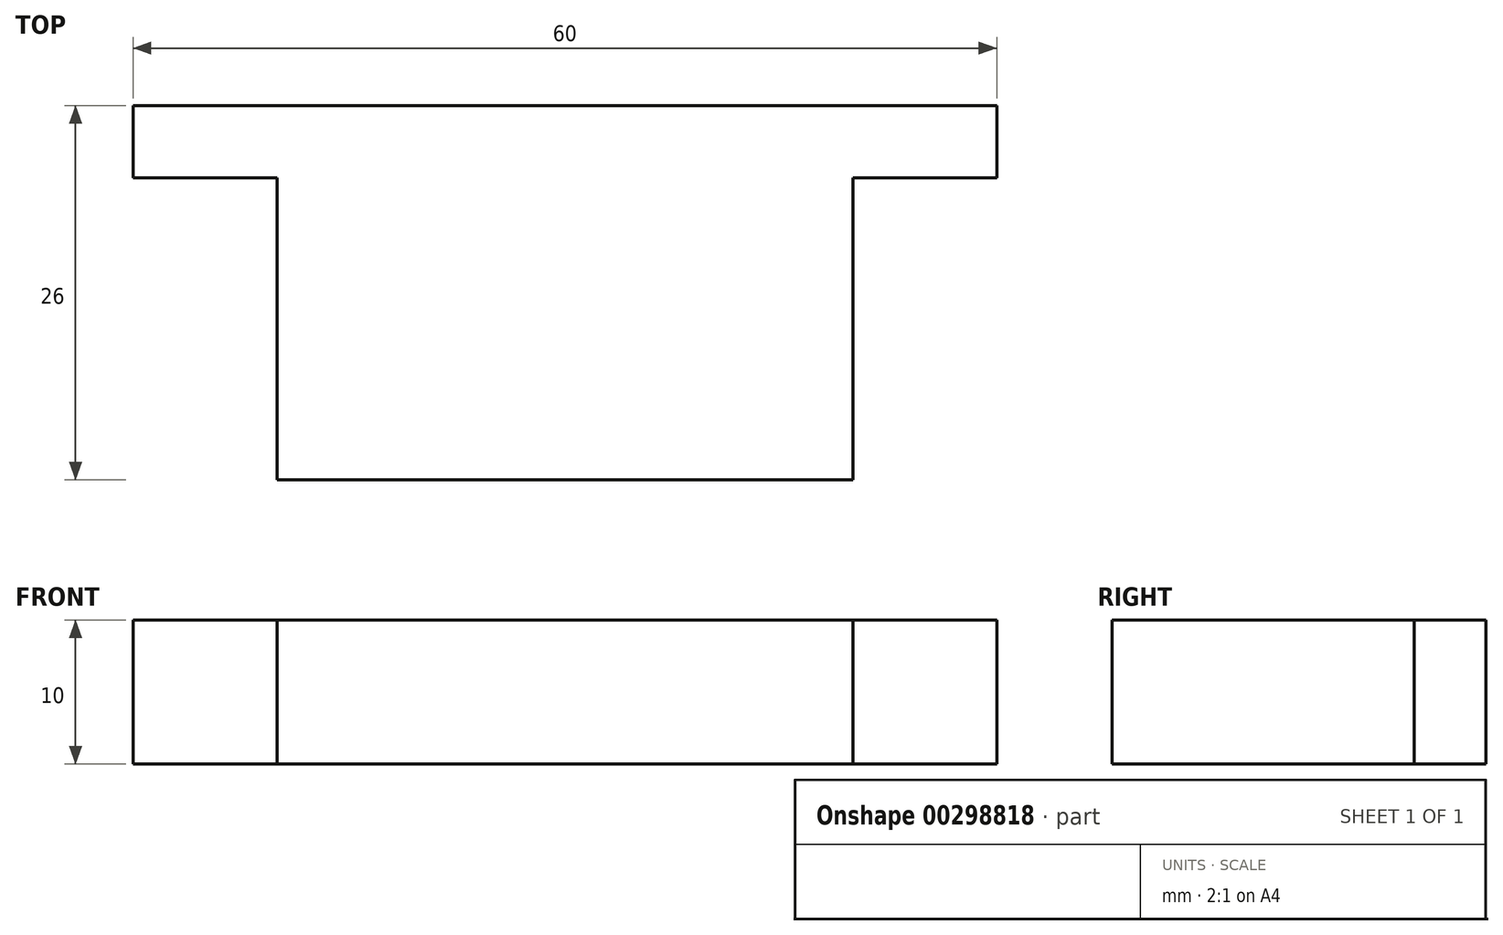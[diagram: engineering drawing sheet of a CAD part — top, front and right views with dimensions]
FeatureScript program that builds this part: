
annotation { "Feature Type Name" : "Feature", "Feature Type Description" : "" }
export const myFeature = defineFeature(function(context is Context, id is Id, definition is map)
    precondition{}
    {
        {
            var Q0;
            Q0=qCreatedBy(makeId("Top.planeOp"),FACE);
            var sketch = newSketch(context, id + "F0", { "sketchPlane" : qUnion([Q0])});
            skLineSegment(sketch, "E0.bottom", {"start": v(-20, 13) * mm, "end": v(20, 13) * mm});
            skLineSegment(sketch, "E0.top", {"start": v(-20, -13) * mm, "end": v(20, -13) * mm});
            skLineSegment(sketch, "E0.left", {"start": v(-20, 8) * mm, "end": v(-20, -13) * mm});
            skLineSegment(sketch, "E0.right", {"start": v(20, 8) * mm, "end": v(20, -13) * mm});
            skPoint(sketch, "E0.middle", {"position": v(0, 0) * mm});
            skLineSegment(sketch, "E1", {"start": v(-20, 8) * mm, "end": v(-30, 8) * mm});
            skLineSegment(sketch, "E2", {"start": v(-30, 8) * mm, "end": v(-30, 13) * mm});
            skLineSegment(sketch, "E3", {"start": v(-30, 13) * mm, "end": v(-20, 13) * mm});
            skLineSegment(sketch, "E4.MirrorCS", {"start": v(20, 8) * mm, "end": v(30, 8) * mm});
            skLineSegment(sketch, "E5.MirrorCS", {"start": v(30, 13) * mm, "end": v(20, 13) * mm});
            skLineSegment(sketch, "E6.MirrorCS", {"start": v(30, 8) * mm, "end": v(30, 13) * mm});
            skSolve(sketch);
        }
        {
            var Q0;
            Q0=makeQuery(id+"F0.imprint","IMPRINT",FACE,{"disambiguationData":[TD([[makeQuery(id+"F0.imprint","IMPRINT",EDGE,{"derivedFrom":sQuery(id+"F0.wireOp",EDGE,"E0.bottom")}),-1.0]])]});
            extrude(context, id + "F1", {"entities" : qUnion([Q0]), "depth" : 10 * mm});
        }
    });
